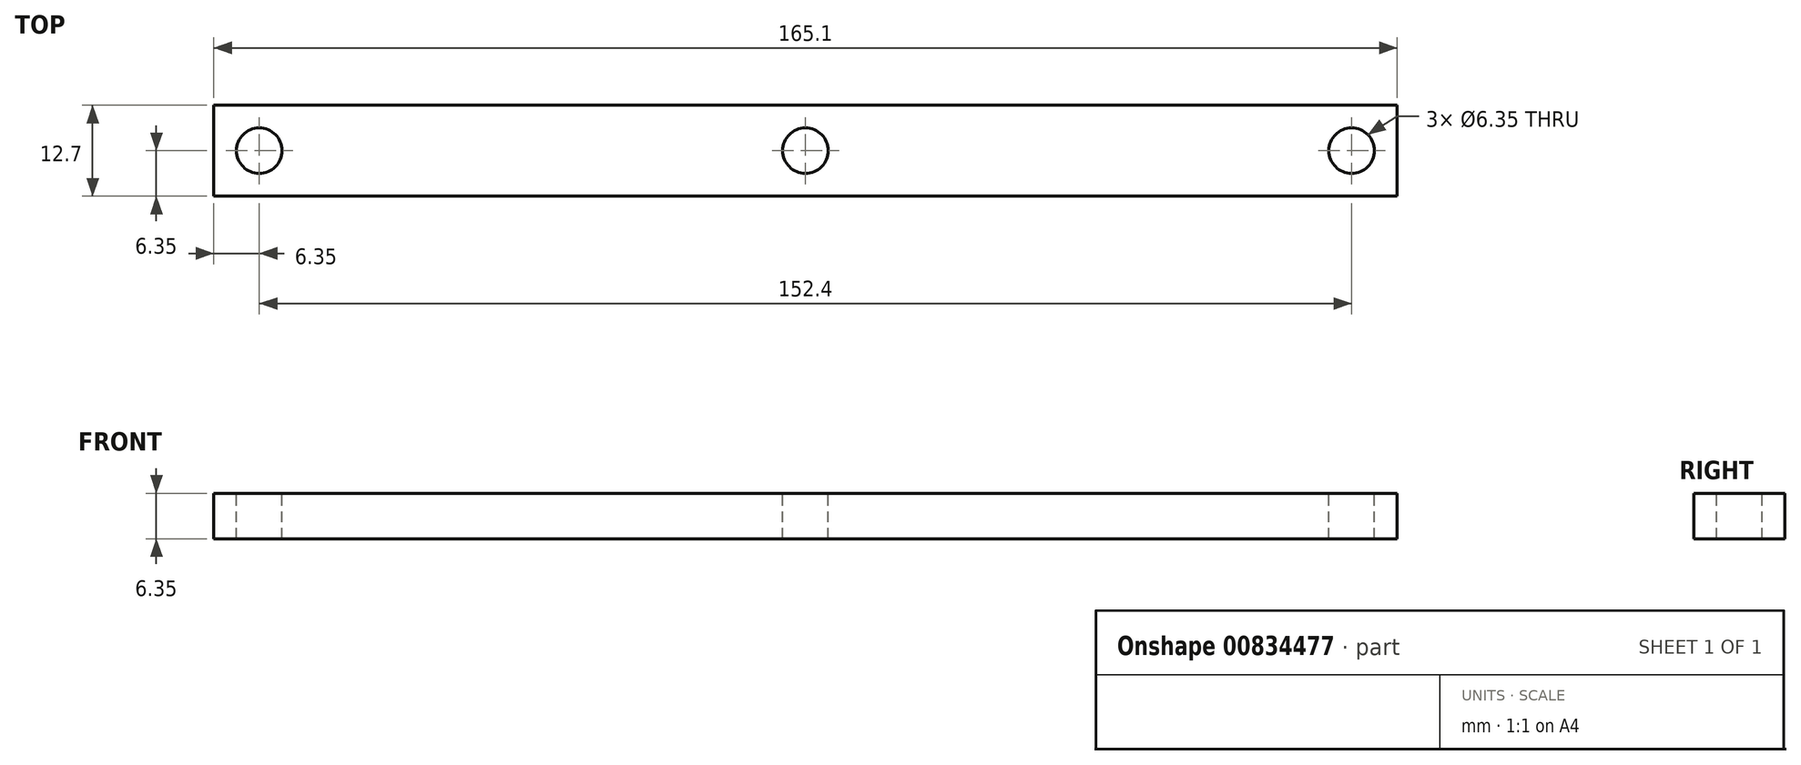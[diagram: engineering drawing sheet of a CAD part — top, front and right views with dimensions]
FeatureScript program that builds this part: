
annotation { "Feature Type Name" : "Feature", "Feature Type Description" : "" }
export const myFeature = defineFeature(function(context is Context, id is Id, definition is map)
    precondition{}
    {
        {
            var Q0;
            Q0=qCreatedBy(makeId("Top.planeOp"),FACE);
            var sketch = newSketch(context, id + "F0", { "sketchPlane" : qUnion([Q0])});
            skLineSegment(sketch, "E0.bottom", {"start": v(0, 0) * mm, "end": v(165.1, 0) * mm});
            skLineSegment(sketch, "E0.top", {"start": v(0, 12.7) * mm, "end": v(165.1, 12.7) * mm});
            skLineSegment(sketch, "E0.left", {"start": v(0, 0) * mm, "end": v(0, 12.7) * mm});
            skLineSegment(sketch, "E0.right", {"start": v(165.1, 0) * mm, "end": v(165.1, 12.7) * mm});
            skSolve(sketch);
        }
        {
            var Q0;
            Q0=makeQuery(id+"F0.imprint","IMPRINT",FACE,{"disambiguationData":[TD([[makeQuery(id+"F0.imprint","IMPRINT",EDGE,{"derivedFrom":sQuery(id+"F0.wireOp",EDGE,"E0.bottom")}),1.0]])]});
            extrude(context, id + "F1", {"entities" : qUnion([Q0]), "depth" : 6.35 * mm, "offsetDistance" : 25.4 * mm});
        }
        {
            var Q0;
            Q0=makeQuery(id+"F1.opExtrude","CAP_FACE",FACE,{"disambiguationData":[OSD([sQuery(id+"F0.wireOp",EDGE,"E0.bottom"),sQuery(id+"F0.wireOp",EDGE,"E0.top"),sQuery(id+"F0.wireOp",EDGE,"E0.left"),sQuery(id+"F0.wireOp",EDGE,"E0.right")])],"isStart":false});
            var sketch = newSketch(context, id + "F2", { "sketchPlane" : qUnion([Q0])});
            skCircle(sketch, "E1", {"center": v(6.35, 6.35) * mm, "radius": 3.18 * mm});
            skCircle(sketch, "E2", {"center": v(82.55, 6.35) * mm, "radius": 3.18 * mm});
            skCircle(sketch, "E3", {"center": v(158.75, 6.35) * mm, "radius": 3.18 * mm});
            skSolve(sketch);
        }
        {
            var Q0;
            Q0=makeQuery(id+"F2.imprint","IMPRINT",FACE,{"disambiguationData":[TD([[makeQuery(id+"F2.imprint","IMPRINT",EDGE,{"derivedFrom":sQuery(id+"F2.wireOp",EDGE,"E1")}),1.0]])]});
            var Q1;
            Q1=makeQuery(id+"F2.imprint","IMPRINT",FACE,{"disambiguationData":[TD([[makeQuery(id+"F2.imprint","IMPRINT",EDGE,{"derivedFrom":sQuery(id+"F2.wireOp",EDGE,"E2")}),1.0]])]});
            var Q2;
            Q2=makeQuery(id+"F2.imprint","IMPRINT",FACE,{"disambiguationData":[TD([[makeQuery(id+"F2.imprint","IMPRINT",EDGE,{"derivedFrom":sQuery(id+"F2.wireOp",EDGE,"E3")}),1.0]])]});
            extrude(context, id + "F3", {"entities" : qUnion([Q0, Q1, Q2]), "operationType" : NewBodyOperationType.REMOVE, "oppositeDirection" : true, "depth" : 25.4 * mm, "offsetDistance" : 25.4 * mm});
        }
    });
